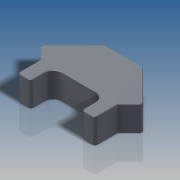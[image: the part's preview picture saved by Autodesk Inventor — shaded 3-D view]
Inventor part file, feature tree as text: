
AUTODESK INVENTOR PART (.ipt)
format: ipt  version: 2016 SP2 (Build 200236200, 236)  size: 154,624 bytes
history: native  units: in
note: dims shown in document units (in); Inventor stores cm internally (conversion verified against a paired STEP export)
features: extrude x1, fillet x1, chamfer x1, sketch x1
ambient origin geometry x8: Origin, YZ Plane, XZ Plane, XY Plane, X Axis, Y Axis, Z Axis, Center Point
bodies: Solid1 (feature_tree)
feature tree (4):
  extrude  "Extrusion1"  Depth=0.1843in
  fillet  "Fillet1"  Radius=0.1071in
  chamfer  "Chamfer1"  Distance=0.4157in
  sketch  "Sketch2"  dims[d0=0.0709in d1=0.1843in d2=0.1071in d3=0.4157in d4=0.1874in d5=0.3669in d6=0.315in d7=0.2047in d8=0.0in d9=0.0236in d10=0.0047in d11=0.0787in d12=45.0deg]
